# Revit family: Faucet_Single_Control-American_Standard-Quince- 4433300.002
name_source: partatom
category: Plumbing Fixtures
units: mm (PartAtom-declared; Revit-internal decimal feet)

## family parameters
Always vertical = No
Cut with Voids When Loaded = No
OmniClass Number = 23.45.55.14
OmniClass Title = Single Faucets
Part Type = Normal
Room Calculation Point = No
Round Connector Dimension = Use Diameter
Shared = Yes
Work Plane-Based = Yes

## types (1)
- 4433300.002
    ADA Compliant = Yes
    Assembly Code = D2020300
    CW Connection = No
    CWFU = 1.5
    Compliance Certifications = These products meet or exceed the following codes and standards: ANSI A117.1, ASME A112.18.1, NSF 61/Section 9 & Annex G, CSA B125
    Default Elevation = 0"
    Description = Quince® Single-Handle Pull-Down Dual-Spray Kitchen Faucet 2.2 gpm/8.3 L/min
    Escutcheon Plate = Yes
    Faucet Height Position = 3/8"
    Finish = Brass-American Standard-002-Polished Chrome
    HW Connection = No
    HWFU = 1.5
    Height = 15"
    Installation Type = Deck Mounted
    Length = 10 1/16"
    Manufacturer = American Standard
    Material = Brass-American Standard-002-Polished Chrome
    Max. Flow Rate = 2.2 gpm (8.3 L/min)
    Min. Flow Rate = 1.5 gpm (5.7 L/min)
    Model = 4433300.002
    Product Documentation Link = https://americanstandard.box.com
    Product Page URL = https://www.americanstandard-us.com
    Revised Date = 09/23/2022
    Tempered Water Connection = Yes
    Tempered Water Connection Diameter = 3/8"
    URL = http://www.americanstandard-us.com
    Vent Connection = No
    WFU = 2
    Waste Connection = No
    Width = 8 3/4"

## geometry (parser evidence)
native form markers: Sweep x5
no freeform markers — native parametric forms only
